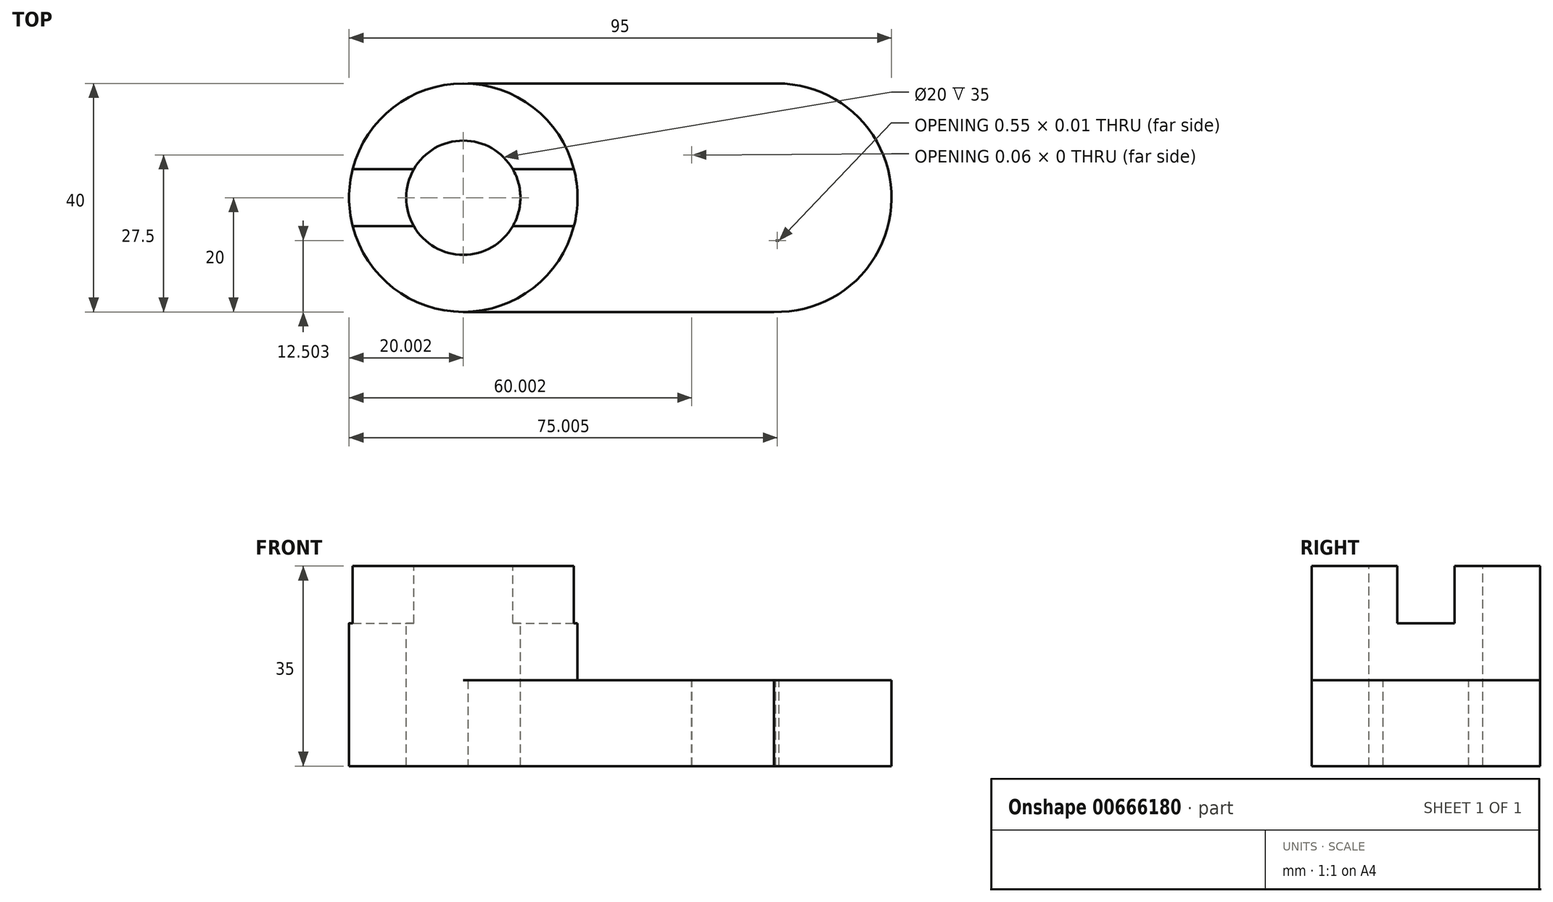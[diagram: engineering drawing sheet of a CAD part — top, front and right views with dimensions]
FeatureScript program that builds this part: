
annotation { "Feature Type Name" : "Feature", "Feature Type Description" : "" }
export const myFeature = defineFeature(function(context is Context, id is Id, definition is map)
    precondition{}
    {
        {
            var Q0;
            Q0=qCreatedBy(makeId("Top.planeOp"),FACE);
            var sketch = newSketch(context, id + "F0", { "sketchPlane" : qUnion([Q0])});
            skArc(sketch, "E0", {"start": v(-26.23, 19.98) * mm, "mid": v(-47.01, 0.4) * mm, "end": v(-27.01, -20) * mm});
            skArc(sketch, "E1", {"start": v(27.4, -20) * mm, "mid": v(47.98, -0.29) * mm, "end": v(27.98, 20) * mm});
            skLineSegment(sketch, "E2", {"start": v(-27.81, 19.98) * mm, "end": v(27.98, 20) * mm});
            skLineSegment(sketch, "E3", {"start": v(27.4, -20) * mm, "end": v(-27.01, -20) * mm});
            skSolve(sketch);
        }
        {
            var Q0;
            Q0 = qSketchRegion(id + "F0", true);
            extrude(context, id + "F1", {"entities" : qUnion([Q0]), "depth" : 15 * mm, "offsetDistance" : 25 * mm});
        }
        {
            var Q0;
            Q0=makeQuery(id+"F1.opExtrude","CAP_FACE",FACE,{"disambiguationData":[OSD([sQuery(id+"F0.wireOp",EDGE,"E0"),sQuery(id+"F0.wireOp",EDGE,"E1"),sQuery(id+"F0.wireOp",EDGE,"E2"),sQuery(id+"F0.wireOp",EDGE,"E3")])],"isStart":false});
            var sketch = newSketch(context, id + "F2", { "sketchPlane" : qUnion([Q0])});
            skCircle(sketch, "E4", {"center": v(-27.02, 0) * mm, "radius": 20 * mm});
            skSolve(sketch);
        }
        {
            var Q0;
            {var subQ0=sQuery(id+"F2.wireOp",EDGE,"E4");var subQ1=makeQuery(id+"F2.imprint","INTERSECT",VERTEX,{"derivedFrom":[makeQuery(id+"F1.opExtrude","CAP_EDGE",EDGE,{"disambiguationData":[OSD([sQuery(id+"F0.wireOp",EDGE,"E2")])],"isStart":false}),subQ0]});Q0=makeQuery(id+"F2.imprint","IMPRINT",FACE,{"disambiguationData":[TD([[makeQuery(id+"F2.imprint","IMPRINT",EDGE,{"disambiguationData":[TD([[subQ1,-1.0]])],"derivedFrom":subQ0}),1.0]])]});}
            extrude(context, id + "F3", {"entities" : qUnion([Q0]), "operationType" : NewBodyOperationType.ADD, "depth" : 20 * mm, "offsetDistance" : 25 * mm});
        }
        {
            var Q0;
            Q0=makeQuery(id+"F3.opExtrude","CAP_FACE",FACE,{"disambiguationData":[OSD([sQuery(id+"F2.wireOp",EDGE,"E4")])],"isStart":false});
            var sketch = newSketch(context, id + "F4", { "sketchPlane" : qUnion([Q0])});
            skCircle(sketch, "E5", {"center": v(-27.02, 0) * mm, "radius": 10 * mm});
            skSolve(sketch);
        }
        {
            var Q0;
            Q0 = qSketchRegion(id + "F4", true);
            extrude(context, id + "F5", {"entities" : qUnion([Q0]), "operationType" : NewBodyOperationType.REMOVE, "oppositeDirection" : true, "depth" : 60.8 * mm, "offsetDistance" : 25 * mm});
        }
        {
            var Q0;
            Q0=makeQuery(id+"F3.opExtrude","CAP_FACE",FACE,{"disambiguationData":[OSD([sQuery(id+"F2.wireOp",EDGE,"E4")])],"isStart":false});
            var sketch = newSketch(context, id + "F6", { "sketchPlane" : qUnion([Q0])});
            skLineSegment(sketch, "E6.bottom", {"start": v(-53.26, 5) * mm, "end": v(6.74, 5) * mm});
            skLineSegment(sketch, "E6.top", {"start": v(-53.26, -5) * mm, "end": v(6.74, -5) * mm});
            skLineSegment(sketch, "E6.left", {"start": v(-53.26, 5) * mm, "end": v(-53.26, -5) * mm});
            skLineSegment(sketch, "E6.right", {"start": v(6.74, 5) * mm, "end": v(6.74, -5) * mm});
            skSolve(sketch);
        }
        {
            var Q0;
            {var subQ0=sQuery(id+"F6.wireOp",EDGE,"E6.left");Q0=makeQuery(id+"F6.imprint","IMPRINT",FACE,{"disambiguationData":[TD([[makeQuery(id+"F6.imprint","IMPRINT",EDGE,{"derivedFrom":subQ0}),1.0]])]});}
            var Q1;
            {var subQ0=sQuery(id+"F6.wireOp",EDGE,"E6.right");Q1=makeQuery(id+"F6.imprint","IMPRINT",FACE,{"disambiguationData":[TD([[makeQuery(id+"F6.imprint","IMPRINT",EDGE,{"derivedFrom":subQ0}),-1.0]])]});}
            var Q2;
            {var subQ0=sQuery(id+"F6.wireOp",EDGE,"E6.bottom");var subQ1=makeQuery(id+"F3.opExtrude","CAP_EDGE",EDGE,{"disambiguationData":[OSD([sQuery(id+"F2.wireOp",EDGE,"E4")])],"isStart":false});var subQ2=makeQuery(id+"F6.imprint","INTERSECT",VERTEX,{"disambiguationData":[OD(0.0)],"derivedFrom":[subQ1,subQ0]});Q2=makeQuery(id+"F6.imprint","IMPRINT",FACE,{"disambiguationData":[TD([[makeQuery(id+"F6.imprint","IMPRINT",EDGE,{"disambiguationData":[TD([[subQ2,-1.0]])],"derivedFrom":subQ0}),-1.0]])]});}
            var Q3;
            {var subQ0=sQuery(id+"F6.wireOp",EDGE,"E6.bottom");var subQ1=makeQuery(id+"F5.boolean.opBoolean","COPY",EDGE,{"derivedFrom":makeQuery(id+"F5.opExtrude","CAP_EDGE",EDGE,{"disambiguationData":[OSD([sQuery(id+"F4.wireOp",EDGE,"E5")])],"isStart":true})});var subQ2=makeQuery(id+"F6.imprint","INTERSECT",VERTEX,{"disambiguationData":[OD(0.0)],"derivedFrom":[subQ1,subQ0]});Q3=makeQuery(id+"F6.imprint","IMPRINT",FACE,{"disambiguationData":[TD([[makeQuery(id+"F6.imprint","IMPRINT",EDGE,{"disambiguationData":[TD([[subQ2,-1.0]])],"derivedFrom":subQ0}),-1.0]])]});}
            var Q4;
            {var subQ0=sQuery(id+"F6.wireOp",EDGE,"E6.bottom");var subQ1=makeQuery(id+"F3.opExtrude","CAP_EDGE",EDGE,{"disambiguationData":[OSD([sQuery(id+"F2.wireOp",EDGE,"E4")])],"isStart":false});var subQ2=makeQuery(id+"F6.imprint","INTERSECT",VERTEX,{"disambiguationData":[OD(1.0)],"derivedFrom":[subQ1,subQ0]});Q4=makeQuery(id+"F6.imprint","IMPRINT",FACE,{"disambiguationData":[TD([[makeQuery(id+"F6.imprint","IMPRINT",EDGE,{"disambiguationData":[TD([[subQ2,1.0]])],"derivedFrom":subQ0}),-1.0]])]});}
            extrude(context, id + "F7", {"entities" : qUnion([Q0, Q1, Q2, Q3, Q4]), "operationType" : NewBodyOperationType.REMOVE, "oppositeDirection" : true, "depth" : 10 * mm, "offsetDistance" : 25 * mm});
        }
        {
            var Q0;
            Q0=makeQuery(id+"F1.opExtrude","CAP_FACE",FACE,{"disambiguationData":[OSD([sQuery(id+"F0.wireOp",EDGE,"E0"),sQuery(id+"F0.wireOp",EDGE,"E1"),sQuery(id+"F0.wireOp",EDGE,"E2"),sQuery(id+"F0.wireOp",EDGE,"E3")])],"isStart":false});
            var sketch = newSketch(context, id + "F8", { "sketchPlane" : qUnion([Q0])});
            skArc(sketch, "E7", {"start": v(27.7, -7.5) * mm, "mid": v(35.48, -0.14) * mm, "end": v(27.98, 7.5) * mm});
            skArc(sketch, "E8", {"start": v(13.01, 7.5) * mm, "mid": v(5.48, 0.01) * mm, "end": v(12.98, -7.5) * mm});
            skLineSegment(sketch, "E9", {"start": v(12.95, 7.5) * mm, "end": v(27.98, 7.5) * mm});
            skLineSegment(sketch, "E10", {"start": v(28.26, -7.5) * mm, "end": v(12.98, -7.5) * mm});
            skSolve(sketch);
        }
        {
            var Q0;
            {var subQ0=sQuery(id+"F8.wireOp",EDGE,"E10");var subQ1=sQuery(id+"F8.wireOp",EDGE,"E7");var subQ2=makeQuery(id+"F8.imprint","INTERSECT",VERTEX,{"disambiguationData":[OD(0.0)],"derivedFrom":[subQ1,subQ0]});Q0=makeQuery(id+"F8.imprint","IMPRINT",FACE,{"disambiguationData":[TD([[makeQuery(id+"F8.imprint","IMPRINT",EDGE,{"disambiguationData":[TD([[subQ2,-1.0]])],"derivedFrom":subQ1}),1.0]])]});}
            var Q1;
            {var subQ4=sQuery(id+"F8.wireOp",EDGE,"E8");Q1=makeQuery(id+"F8.imprint","IMPRINT",FACE,{"disambiguationData":[TD([[makeQuery(id+"F8.imprint","IMPRINT",EDGE,{"derivedFrom":subQ4}),1.0]])]});}
            extrude(context, id + "F9", {"entities" : qUnion([Q0, Q1]), "operationType" : NewBodyOperationType.REMOVE, "oppositeDirection" : true, "depth" : 33.1 * mm, "offsetDistance" : 25 * mm});
        }
    });
